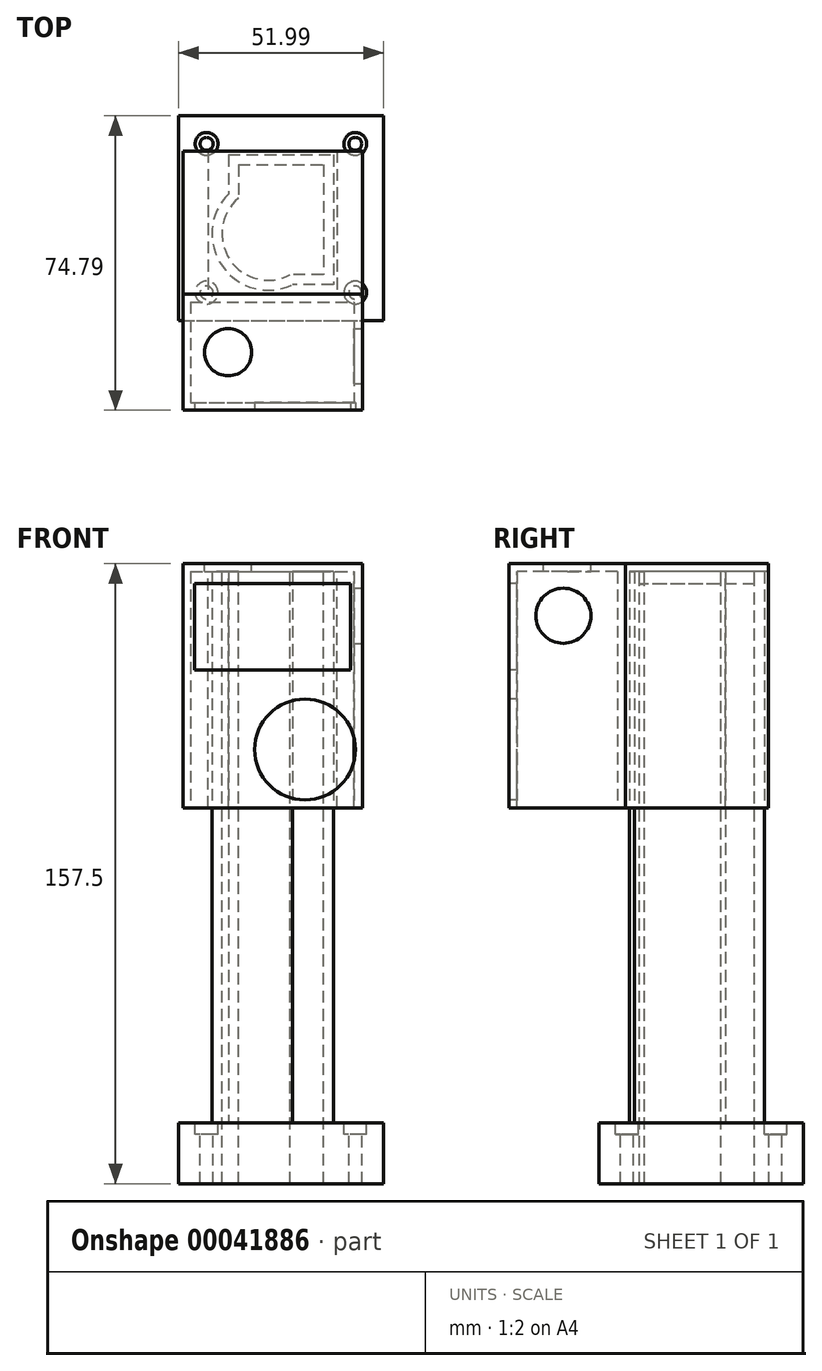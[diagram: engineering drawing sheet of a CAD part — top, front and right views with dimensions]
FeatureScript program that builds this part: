
annotation { "Feature Type Name" : "Feature", "Feature Type Description" : "" }
export const myFeature = defineFeature(function(context is Context, id is Id, definition is map)
    precondition{}
    {
        {
            var Q0;
            Q0=qCreatedBy(makeId("Top.planeOp"),FACE);
            var sketch = newSketch(context, id + "F0", { "sketchPlane" : qUnion([Q0])});
            skLineSegment(sketch, "E0.bottom", {"start": v(0, 0) * mm, "end": v(52, 0) * mm});
            skLineSegment(sketch, "E0.top", {"start": v(0, 52) * mm, "end": v(52, 52) * mm});
            skLineSegment(sketch, "E0.left", {"start": v(0, 0) * mm, "end": v(0, 52) * mm});
            skLineSegment(sketch, "E0.right", {"start": v(52, 0) * mm, "end": v(52, 52) * mm});
            skSolve(sketch);
        }
        {
            var Q0;
            Q0 = qSketchRegion(id + "F0", true);
            extrude(context, id + "F1", {"entities" : qUnion([Q0]), "depth" : 15.5 * mm});
        }
        {
            var Q0;
            Q0=makeQuery(id+"F1.opExtrude","CAP_FACE",FACE,{"disambiguationData":[OSD([sQuery(id+"F0.wireOp",EDGE,"E0.bottom"),sQuery(id+"F0.wireOp",EDGE,"E0.top"),sQuery(id+"F0.wireOp",EDGE,"E0.left"),sQuery(id+"F0.wireOp",EDGE,"E0.right")])],"isStart":false});
            var sketch = newSketch(context, id + "F2", { "sketchPlane" : qUnion([Q0])});
            skCircle(sketch, "E1", {"center": v(7.11, 44.88) * mm, "radius": 2.9 * mm});
            skCircle(sketch, "E2", {"center": v(44.88, 44.88) * mm, "radius": 2.9 * mm});
            skCircle(sketch, "E3", {"center": v(7.11, 7.11) * mm, "radius": 2.9 * mm});
            skCircle(sketch, "E4", {"center": v(44.88, 7.11) * mm, "radius": 2.9 * mm});
            skSolve(sketch);
        }
        {
            var Q0;
            Q0 = qSketchRegion(id + "F2", true);
            extrude(context, id + "F3", {"entities" : qUnion([Q0]), "operationType" : NewBodyOperationType.REMOVE, "oppositeDirection" : true, "depth" : 3 * mm});
        }
        {
            var Q0;
            Q0=makeQuery(id+"F3.boolean.opBoolean","COPY",FACE,{"derivedFrom":makeQuery(id+"F3.opExtrude","CAP_FACE",FACE,{"disambiguationData":[OSD([sQuery(id+"F2.wireOp",EDGE,"E1")])],"isStart":false})});
            var sketch = newSketch(context, id + "F4", { "sketchPlane" : qUnion([Q0])});
            skCircle(sketch, "E5", {"center": v(7.11, 44.88) * mm, "radius": 1.65 * mm});
            skSolve(sketch);
        }
        {
            var Q0;
            Q0 = qSketchRegion(id + "F4", true);
            extrude(context, id + "F5", {"entities" : qUnion([Q0]), "operationType" : NewBodyOperationType.REMOVE, "endBound" : BoundingType.THROUGH_ALL, "oppositeDirection" : true, "depth" : 25.4 * mm});
        }
        {
            var Q0;
            Q0=makeQuery(id+"F3.boolean.opBoolean","COPY",FACE,{"derivedFrom":makeQuery(id+"F3.opExtrude","CAP_FACE",FACE,{"disambiguationData":[OSD([sQuery(id+"F2.wireOp",EDGE,"E2")])],"isStart":false})});
            var sketch = newSketch(context, id + "F6", { "sketchPlane" : qUnion([Q0])});
            skCircle(sketch, "E6", {"center": v(44.88, 44.88) * mm, "radius": 1.65 * mm});
            skSolve(sketch);
        }
        {
            var Q0;
            Q0 = qSketchRegion(id + "F6", true);
            extrude(context, id + "F7", {"entities" : qUnion([Q0]), "operationType" : NewBodyOperationType.REMOVE, "endBound" : BoundingType.THROUGH_ALL, "oppositeDirection" : true, "depth" : 25.4 * mm});
        }
        {
            var Q0;
            Q0=makeQuery(id+"F3.boolean.opBoolean","COPY",FACE,{"derivedFrom":makeQuery(id+"F3.opExtrude","CAP_FACE",FACE,{"disambiguationData":[OSD([sQuery(id+"F2.wireOp",EDGE,"E3")])],"isStart":false})});
            var sketch = newSketch(context, id + "F8", { "sketchPlane" : qUnion([Q0])});
            skCircle(sketch, "E7", {"center": v(7.11, 7.11) * mm, "radius": 1.65 * mm});
            skSolve(sketch);
        }
        {
            var Q0;
            Q0 = qSketchRegion(id + "F8", true);
            extrude(context, id + "F9", {"entities" : qUnion([Q0]), "operationType" : NewBodyOperationType.REMOVE, "endBound" : BoundingType.THROUGH_ALL, "oppositeDirection" : true, "depth" : 25.4 * mm});
        }
        {
            var Q0;
            Q0=makeQuery(id+"F3.boolean.opBoolean","COPY",FACE,{"derivedFrom":makeQuery(id+"F3.opExtrude","CAP_FACE",FACE,{"disambiguationData":[OSD([sQuery(id+"F2.wireOp",EDGE,"E4")])],"isStart":false})});
            var sketch = newSketch(context, id + "F10", { "sketchPlane" : qUnion([Q0])});
            skCircle(sketch, "E8", {"center": v(44.88, 7.11) * mm, "radius": 1.65 * mm});
            skSolve(sketch);
        }
        {
            var Q0;
            Q0 = qSketchRegion(id + "F10", true);
            extrude(context, id + "F11", {"entities" : qUnion([Q0]), "operationType" : NewBodyOperationType.REMOVE, "endBound" : BoundingType.THROUGH_ALL, "oppositeDirection" : true, "depth" : 25.4 * mm});
        }
        {
            var Q0;
            Q0=makeQuery(id+"F1.opExtrude","CAP_FACE",FACE,{"disambiguationData":[OSD([sQuery(id+"F0.wireOp",EDGE,"E0.bottom"),sQuery(id+"F0.wireOp",EDGE,"E0.top"),sQuery(id+"F0.wireOp",EDGE,"E0.left"),sQuery(id+"F0.wireOp",EDGE,"E0.right")])],"isStart":false});
            var sketch = newSketch(context, id + "F12", { "sketchPlane" : qUnion([Q0])});
            skPoint(sketch, "E9.centerSnap0", {"position": v(18.87, 22.05) * mm});
            skPoint(sketch, "E10.orphan", {"position": v(18.87, 32.5) * mm});
            skPoint(sketch, "E11.orphan", {"position": v(18.87, 11.6) * mm});
            skPoint(sketch, "E12.end.orphan", {"position": v(15.39, 32.35) * mm});
            skLineSegment(sketch, "E13", {"start": v(15.16, 32.35) * mm, "end": v(15.39, 32.35) * mm});
            skLineSegment(sketch, "E14.0", {"start": v(39.3, 42.09) * mm, "end": v(39.3, 9.07) * mm});
            skLineSegment(sketch, "E14.1", {"start": v(12.62, 42.09) * mm, "end": v(39.3, 42.09) * mm});
            skLineSegment(sketch, "E14.2", {"start": v(39.3, 9.07) * mm, "end": v(28.94, 9.07) * mm});
            skArc(sketch, "E14.3", {"start": v(12.62, 32.14) * mm, "mid": v(11.11, 13.76) * mm, "end": v(28.94, 9.07) * mm});
            skLineSegment(sketch, "E14.4", {"start": v(12.62, 42.09) * mm, "end": v(12.62, 32.14) * mm});
            skSolve(sketch);
        }
        {
            var Q0;
            Q0 = qSketchRegion(id + "F12", true);
            extrude(context, id + "F13", {"entities" : qUnion([Q0]), "operationType" : NewBodyOperationType.ADD, "depth" : 140 * mm});
        }
        {
            var Q0;
            Q0=makeQuery(id+"F13.opExtrude","CAP_FACE",FACE,{"disambiguationData":[OSD([sQuery(id+"F12.wireOp",EDGE,"E14.0"),sQuery(id+"F12.wireOp",EDGE,"E14.1"),sQuery(id+"F12.wireOp",EDGE,"E14.2"),sQuery(id+"F12.wireOp",EDGE,"E14.3"),sQuery(id+"F12.wireOp",EDGE,"E14.4")])],"isStart":false});
            var sketch = newSketch(context, id + "F14", { "sketchPlane" : qUnion([Q0])});
            skPoint(sketch, "E15.center.orphan", {"position": v(22.83, 22.05) * mm});
            skLineSegment(sketch, "E16.0", {"start": v(36.75, 39.55) * mm, "end": v(36.75, 11.6) * mm});
            skLineSegment(sketch, "E16.1", {"start": v(15.16, 39.55) * mm, "end": v(36.75, 39.55) * mm});
            skLineSegment(sketch, "E16.2", {"start": v(36.75, 11.6) * mm, "end": v(28.35, 11.6) * mm});
            skArc(sketch, "E16.3", {"start": v(15.16, 31.04) * mm, "mid": v(13.06, 15.42) * mm, "end": v(28.35, 11.6) * mm});
            skLineSegment(sketch, "E16.4", {"start": v(15.16, 39.55) * mm, "end": v(15.16, 31.04) * mm});
            skSolve(sketch);
        }
        {
            var Q0;
            Q0 = qSketchRegion(id + "F14", true);
            extrude(context, id + "F15", {"entities" : qUnion([Q0]), "operationType" : NewBodyOperationType.REMOVE, "endBound" : BoundingType.THROUGH_ALL, "oppositeDirection" : true, "depth" : 25.4 * mm});
        }
        {
            var Q0;
            Q0=makeQuery(id+"F13.opExtrude","CAP_FACE",FACE,{"disambiguationData":[OSD([sQuery(id+"F12.wireOp",EDGE,"E14.0"),sQuery(id+"F12.wireOp",EDGE,"E14.1"),sQuery(id+"F12.wireOp",EDGE,"E14.2"),sQuery(id+"F12.wireOp",EDGE,"E14.3"),sQuery(id+"F12.wireOp",EDGE,"E14.4")])],"isStart":false});
            var sketch = newSketch(context, id + "F16", { "sketchPlane" : qUnion([Q0])});
            skLineSegment(sketch, "E17", {"start": v(15.16, 39.55) * mm, "end": v(36.75, 39.55) * mm});
            skLineSegment(sketch, "E18", {"start": v(36.75, 39.55) * mm, "end": v(36.75, 11.6) * mm});
            skLineSegment(sketch, "E19", {"start": v(36.75, 11.6) * mm, "end": v(28.35, 11.6) * mm});
            skLineSegment(sketch, "E20", {"start": v(15.16, 39.55) * mm, "end": v(15.16, 31.04) * mm});
            skArc(sketch, "E21", {"start": v(15.16, 31.04) * mm, "mid": v(13.06, 15.42) * mm, "end": v(28.35, 11.6) * mm});
            skSolve(sketch);
        }
        {
            var Q0;
            Q0 = qSketchRegion(id + "F16", true);
            extrude(context, id + "F17", {"entities" : qUnion([Q0]), "oppositeDirection" : true, "depth" : 3.1 * mm});
        }
        {
            var Q0;
            Q0=makeQuery(id+"F17.opExtrude","CAP_FACE",FACE,{"disambiguationData":[OSD([sQuery(id+"F16.wireOp",EDGE,"E17"),sQuery(id+"F16.wireOp",EDGE,"E18"),sQuery(id+"F16.wireOp",EDGE,"E19"),sQuery(id+"F16.wireOp",EDGE,"E20"),sQuery(id+"F16.wireOp",EDGE,"E21")])],"isStart":true});
            var sketch = newSketch(context, id + "F18", { "sketchPlane" : qUnion([Q0])});
            skLineSegment(sketch, "E22.bottom", {"start": v(7.48, 43.09) * mm, "end": v(40.3, 43.09) * mm});
            skLineSegment(sketch, "E22.top", {"start": v(7.48, 6.7) * mm, "end": v(40.3, 6.7) * mm});
            skLineSegment(sketch, "E22.left", {"start": v(7.48, 43.09) * mm, "end": v(7.48, 6.7) * mm});
            skLineSegment(sketch, "E22.right", {"start": v(40.3, 43.09) * mm, "end": v(40.3, 6.7) * mm});
            skLineSegment(sketch, "E23", {"start": v(12.62, 42.09) * mm, "end": v(39.3, 42.09) * mm});
            skLineSegment(sketch, "E24", {"start": v(39.3, 42.09) * mm, "end": v(39.3, 9.07) * mm});
            skPoint(sketch, "E25.center.orphan", {"position": v(22.83, 22.05) * mm});
            skArc(sketch, "E26", {"start": v(12.62, 32.14) * mm, "mid": v(11.11, 13.76) * mm, "end": v(28.94, 9.07) * mm});
            skLineSegment(sketch, "E27", {"start": v(12.62, 42.09) * mm, "end": v(12.62, 32.14) * mm});
            skLineSegment(sketch, "E28", {"start": v(39.3, 9.07) * mm, "end": v(28.94, 9.07) * mm});
            skPoint(sketch, "E29.orphan", {"position": v(12.62, 9.07) * mm});
            skSolve(sketch);
        }
        {
            var Q0;
            Q0 = qSketchRegion(id + "F18", true);
            extrude(context, id + "F19", {"entities" : qUnion([Q0]), "oppositeDirection" : true, "depth" : 60 * mm});
        }
        {
            var Q0;
            Q0=makeQuery(id+"F19.opExtrude","SWEPT_FACE",FACE,{"disambiguationData":[OSD([sQuery(id+"F18.wireOp",EDGE,"E22.top")])]});
            var sketch = newSketch(context, id + "F20", { "sketchPlane" : qUnion([Q0])});
            skLineSegment(sketch, "E30.top", {"start": v(1.09, 95.5) * mm, "end": v(46.69, 95.5) * mm});
            skPoint(sketch, "E30.left.start.orphan", {"position": v(1.09, 155.5) * mm});
            skLineSegment(sketch, "E31", {"start": v(1.09, 95.5) * mm, "end": v(1.09, 157.5) * mm});
            skLineSegment(sketch, "E32", {"start": v(1.09, 157.5) * mm, "end": v(46.69, 157.5) * mm});
            skLineSegment(sketch, "E33", {"start": v(46.69, 157.5) * mm, "end": v(46.69, 95.5) * mm});
            skSolve(sketch);
        }
        {
            var Q0;
            Q0 = qSketchRegion(id + "F20", true);
            extrude(context, id + "F21", {"entities" : qUnion([Q0]), "depth" : 29.5 * mm});
        }
        {
            var Q0;
            Q0=makeQuery(id+"F21.opExtrude","SWEPT_FACE",FACE,{"disambiguationData":[OSD([sQuery(id+"F20.wireOp",EDGE,"E30.top")])]});
            var sketch = newSketch(context, id + "F22", { "sketchPlane" : qUnion([Q0])});
            skLineSegment(sketch, "E34.top", {"start": v(3.09, 20.8) * mm, "end": v(44.59, 20.8) * mm});
            skLineSegment(sketch, "E34.left", {"start": v(3.09, -4.7) * mm, "end": v(3.09, 20.8) * mm});
            skLineSegment(sketch, "E34.right", {"start": v(44.59, -4.7) * mm, "end": v(44.59, 20.8) * mm});
            skLineSegment(sketch, "E35", {"start": v(3.09, -4.7) * mm, "end": v(44.59, -4.7) * mm});
            skSolve(sketch);
        }
        {
            var Q0;
            Q0 = qSketchRegion(id + "F22", true);
            extrude(context, id + "F23", {"entities" : qUnion([Q0]), "operationType" : NewBodyOperationType.REMOVE, "oppositeDirection" : true, "depth" : 60 * mm});
        }
        {
            var Q0;
            Q0=makeQuery(id+"F21.opExtrude","CAP_FACE",FACE,{"disambiguationData":[OSD([sQuery(id+"F20.wireOp",EDGE,"E30.top"),sQuery(id+"F20.wireOp",EDGE,"E31"),sQuery(id+"F20.wireOp",EDGE,"E32"),sQuery(id+"F20.wireOp",EDGE,"E33")])],"isStart":false});
            var sketch = newSketch(context, id + "F24", { "sketchPlane" : qUnion([Q0])});
            skLineSegment(sketch, "E36.bottom", {"start": v(4.09, 152.5) * mm, "end": v(43.69, 152.5) * mm});
            skLineSegment(sketch, "E36.top", {"start": v(4.09, 130.5) * mm, "end": v(43.69, 130.5) * mm});
            skLineSegment(sketch, "E36.left", {"start": v(4.09, 152.5) * mm, "end": v(4.09, 130.5) * mm});
            skLineSegment(sketch, "E36.right", {"start": v(43.69, 152.5) * mm, "end": v(43.69, 130.5) * mm});
            skCircle(sketch, "E37", {"center": v(32.11, 110.32) * mm, "radius": 12.81 * mm});
            skSolve(sketch);
        }
        {
            var Q0;
            Q0 = qSketchRegion(id + "F24", true);
            extrude(context, id + "F25", {"entities" : qUnion([Q0]), "operationType" : NewBodyOperationType.REMOVE, "oppositeDirection" : true, "depth" : 2 * mm});
        }
        {
            var Q0;
            Q0=makeQuery(id+"F21.opExtrude","SWEPT_FACE",FACE,{"disambiguationData":[OSD([sQuery(id+"F20.wireOp",EDGE,"E33")])]});
            var sketch = newSketch(context, id + "F26", { "sketchPlane" : qUnion([Q0])});
            skCircle(sketch, "E38", {"center": v(-9.05, 144.3) * mm, "radius": 7 * mm});
            skSolve(sketch);
        }
        {
            var Q0;
            Q0 = qSketchRegion(id + "F26", true);
            extrude(context, id + "F27", {"entities" : qUnion([Q0]), "operationType" : NewBodyOperationType.REMOVE, "oppositeDirection" : true, "depth" : 25 * mm});
        }
        {
            var Q0;
            Q0=makeQuery(id+"F21.opExtrude","SWEPT_FACE",FACE,{"disambiguationData":[OSD([sQuery(id+"F20.wireOp",EDGE,"E32")])]});
            var sketch = newSketch(context, id + "F28", { "sketchPlane" : qUnion([Q0])});
            skCircle(sketch, "E39", {"center": v(12.59, -8.05) * mm, "radius": 6 * mm});
            skSolve(sketch);
        }
        {
            var Q0;
            Q0 = qSketchRegion(id + "F28", true);
            extrude(context, id + "F29", {"entities" : qUnion([Q0]), "operationType" : NewBodyOperationType.REMOVE, "oppositeDirection" : true, "depth" : 25 * mm});
        }
        {
            var Q0;
            Q0=makeQuery(id+"F21.opExtrude","CAP_FACE",FACE,{"disambiguationData":[OSD([sQuery(id+"F20.wireOp",EDGE,"E30.top"),sQuery(id+"F20.wireOp",EDGE,"E31"),sQuery(id+"F20.wireOp",EDGE,"E32"),sQuery(id+"F20.wireOp",EDGE,"E33")])],"isStart":true});
            var sketch = newSketch(context, id + "F30", { "sketchPlane" : qUnion([Q0])});
            skLineSegment(sketch, "E40.0", {"start": v(-46.69, 157.5) * mm, "end": v(-46.69, 95.5) * mm});
            skLineSegment(sketch, "E41.0", {"start": v(-1.09, 157.5) * mm, "end": v(-46.69, 157.5) * mm});
            skLineSegment(sketch, "E42.0", {"start": v(-1.09, 95.5) * mm, "end": v(-46.69, 95.5) * mm});
            skLineSegment(sketch, "E43.0", {"start": v(-40.3, 95.5) * mm, "end": v(-40.3, 155.5) * mm});
            skLineSegment(sketch, "E44.0", {"start": v(-7.48, 95.5) * mm, "end": v(-7.48, 155.5) * mm});
            skLineSegment(sketch, "E45.0", {"start": v(-1.09, 95.5) * mm, "end": v(-1.09, 157.5) * mm});
            skLineSegment(sketch, "E46.0", {"start": v(-7.48, 155.5) * mm, "end": v(-40.3, 155.5) * mm});
            skSolve(sketch);
        }
        {
            var Q0;
            {var subQ3=sQuery(id+"F30.wireOp",EDGE,"E40.0");Q0=makeQuery(id+"F30.imprint","IMPRINT",FACE,{"disambiguationData":[TD([[makeQuery(id+"F30.imprint","IMPRINT",EDGE,{"derivedFrom":subQ3}),1.0]])]});}
            extrude(context, id + "F31", {"entities" : qUnion([Q0]), "depth" : 36.4 * mm});
        }
    });
